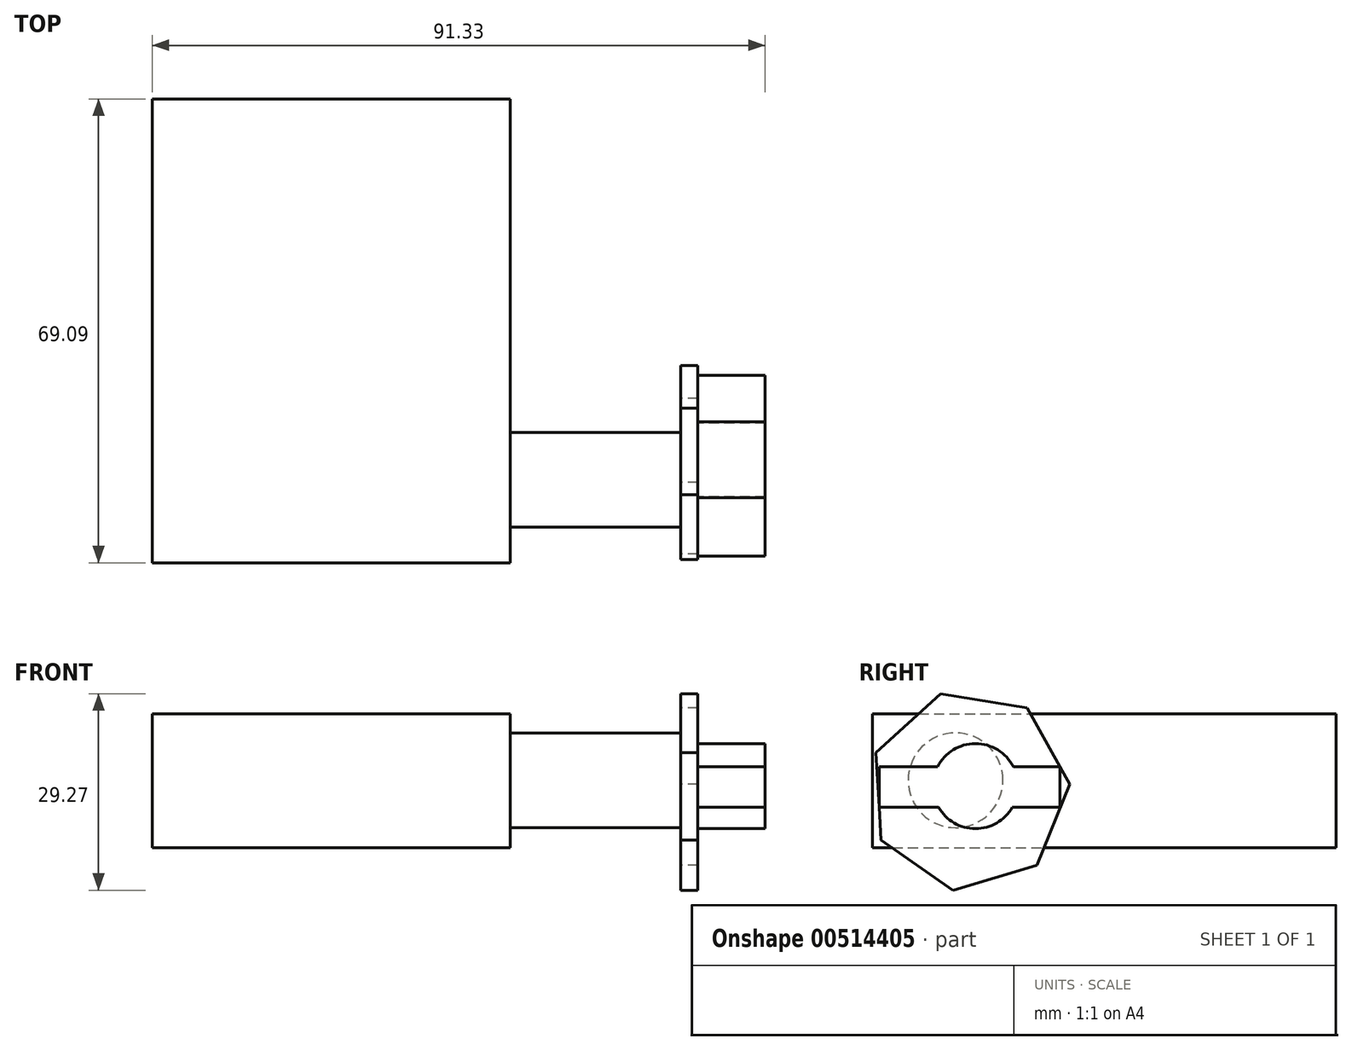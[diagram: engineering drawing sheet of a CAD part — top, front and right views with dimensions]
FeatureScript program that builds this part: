
annotation { "Feature Type Name" : "Feature", "Feature Type Description" : "" }
export const myFeature = defineFeature(function(context is Context, id is Id, definition is map)
    precondition{}
    {
        {
            var Q0;
            Q0=qCreatedBy(makeId("Front.planeOp"),FACE);
            var sketch = newSketch(context, id + "F0", { "sketchPlane" : qUnion([Q0])});
            skLineSegment(sketch, "E0.bottom", {"start": v(-40.49, 8.66) * mm, "end": v(12.87, 8.66) * mm});
            skLineSegment(sketch, "E0.top", {"start": v(-40.49, 28.64) * mm, "end": v(12.87, 28.64) * mm});
            skLineSegment(sketch, "E0.left", {"start": v(-40.49, 8.66) * mm, "end": v(-40.49, 28.64) * mm});
            skLineSegment(sketch, "E0.right", {"start": v(12.87, 8.66) * mm, "end": v(12.87, 28.64) * mm});
            skSolve(sketch);
        }
        {
            var Q0;
            Q0 = qSketchRegion(id + "F0", true);
            extrude(context, id + "F1", {"entities" : qUnion([Q0]), "depth" : 69.1 * mm});
        }
        {
            var Q0;
            Q0=makeQuery(id+"F1.opExtrude","SWEPT_FACE",FACE,{"disambiguationData":[OSD([sQuery(id+"F0.wireOp",EDGE,"E0.right")])]});
            var sketch = newSketch(context, id + "F2", { "sketchPlane" : qUnion([Q0])});
            skCircle(sketch, "E1", {"center": v(-56.73, 18.72) * mm, "radius": 7.06 * mm});
            skSolve(sketch);
        }
        {
            var Q0;
            Q0 = qSketchRegion(id + "F2", true);
            extrude(context, id + "F3", {"entities" : qUnion([Q0]), "operationType" : NewBodyOperationType.ADD, "depth" : 25.4 * mm});
        }
        {
            var Q0;
            Q0=makeQuery(id+"F3.opExtrude","CAP_FACE",FACE,{"disambiguationData":[OSD([sQuery(id+"F2.wireOp",EDGE,"E1")])],"isStart":false});
            var sketch = newSketch(context, id + "F4", { "sketchPlane" : qUnion([Q0])});
            skCircle(sketch, "E2.cCircle", {"center": v(-54.7, 17.2) * mm, "radius": 13.55 * mm, "construction": true});
            skLineSegment(sketch, "E2.0", {"start": v(-58.95, 31.62) * mm, "end": v(-46.07, 29.51) * mm});
            skLineSegment(sketch, "E2.1", {"start": v(-46.07, 29.51) * mm, "end": v(-39.69, 18.13) * mm});
            skLineSegment(sketch, "E2.2", {"start": v(-39.69, 18.13) * mm, "end": v(-44.6, 6.04) * mm});
            skLineSegment(sketch, "E2.3", {"start": v(-44.6, 6.04) * mm, "end": v(-57.12, 2.35) * mm});
            skLineSegment(sketch, "E2.4", {"start": v(-57.12, 2.35) * mm, "end": v(-67.81, 9.84) * mm});
            skLineSegment(sketch, "E2.5", {"start": v(-67.81, 9.84) * mm, "end": v(-68.62, 22.86) * mm});
            skLineSegment(sketch, "E2.6", {"start": v(-68.62, 22.86) * mm, "end": v(-58.95, 31.62) * mm});
            skPoint(sketch, "E2.0.midPoint", {"position": v(-52.5, 30.56) * mm});
            skSolve(sketch);
        }
        {
            var Q0;
            Q0 = qSketchRegion(id + "F4", true);
            extrude(context, id + "F5", {"entities" : qUnion([Q0]), "operationType" : NewBodyOperationType.ADD, "depth" : 2.54 * mm});
        }
        {
            var Q0;
            Q0=makeQuery(id+"F5.opExtrude","CAP_FACE",FACE,{"disambiguationData":[OSD([sQuery(id+"F4.wireOp",EDGE,"E2.0"),sQuery(id+"F4.wireOp",EDGE,"E2.1"),sQuery(id+"F4.wireOp",EDGE,"E2.2"),sQuery(id+"F4.wireOp",EDGE,"E2.3"),sQuery(id+"F4.wireOp",EDGE,"E2.4"),sQuery(id+"F4.wireOp",EDGE,"E2.5"),sQuery(id+"F4.wireOp",EDGE,"E2.6")])],"isStart":false});
            var sketch = newSketch(context, id + "F6", { "sketchPlane" : qUnion([Q0])});
            skCircle(sketch, "E3", {"center": v(-53.77, 17.85) * mm, "radius": 6.34 * mm});
            skLineSegment(sketch, "E4.bottom", {"start": v(-68.11, 14.68) * mm, "end": v(-41.15, 14.68) * mm});
            skLineSegment(sketch, "E4.top", {"start": v(-68.11, 20.74) * mm, "end": v(-41.15, 20.74) * mm});
            skLineSegment(sketch, "E4.left", {"start": v(-68.11, 14.68) * mm, "end": v(-68.11, 20.74) * mm});
            skLineSegment(sketch, "E4.right", {"start": v(-41.15, 14.68) * mm, "end": v(-41.15, 20.74) * mm});
            skSolve(sketch);
        }
        {
            var Q0;
            {var subQ0=sQuery(id+"F6.wireOp",EDGE,"E4.bottom");var subQ1=sQuery(id+"F6.wireOp",EDGE,"E3");var subQ2=makeQuery(id+"F6.imprint","INTERSECT",VERTEX,{"disambiguationData":[OD(0.0)],"derivedFrom":[subQ1,subQ0]});Q0=makeQuery(id+"F6.imprint","IMPRINT",FACE,{"disambiguationData":[TD([[makeQuery(id+"F6.imprint","IMPRINT",EDGE,{"disambiguationData":[TD([[subQ2,-1.0]])],"derivedFrom":subQ1}),1.0]])]});}
            var Q1;
            {var subQ5=sQuery(id+"F6.wireOp",EDGE,"E4.right");Q1=makeQuery(id+"F6.imprint","IMPRINT",FACE,{"disambiguationData":[TD([[makeQuery(id+"F6.imprint","IMPRINT",EDGE,{"derivedFrom":subQ5}),1.0]])]});}
            var Q2;
            {var subQ5=sQuery(id+"F6.wireOp",EDGE,"E4.left");Q2=makeQuery(id+"F6.imprint","IMPRINT",FACE,{"disambiguationData":[TD([[makeQuery(id+"F6.imprint","IMPRINT",EDGE,{"derivedFrom":subQ5}),-1.0]])]});}
            var Q3;
            {var subQ0=sQuery(id+"F6.wireOp",EDGE,"E4.top");var subQ1=sQuery(id+"F6.wireOp",EDGE,"E3");var subQ2=makeQuery(id+"F6.imprint","INTERSECT",VERTEX,{"disambiguationData":[OD(0.0)],"derivedFrom":[subQ1,subQ0]});Q3=makeQuery(id+"F6.imprint","IMPRINT",FACE,{"disambiguationData":[TD([[makeQuery(id+"F6.imprint","IMPRINT",EDGE,{"disambiguationData":[TD([[subQ2,-1.0]])],"derivedFrom":subQ1}),1.0]])]});}
            var Q4;
            {var subQ0=sQuery(id+"F6.wireOp",EDGE,"E4.top");var subQ1=sQuery(id+"F6.wireOp",EDGE,"E3");var subQ2=makeQuery(id+"F6.imprint","INTERSECT",VERTEX,{"disambiguationData":[OD(0.0)],"derivedFrom":[subQ1,subQ0]});Q4=makeQuery(id+"F6.imprint","IMPRINT",FACE,{"disambiguationData":[TD([[makeQuery(id+"F6.imprint","IMPRINT",EDGE,{"disambiguationData":[TD([[subQ2,1.0]])],"derivedFrom":subQ1}),1.0]])]});}
            extrude(context, id + "F7", {"entities" : qUnion([Q0, Q1, Q2, Q3, Q4]), "operationType" : NewBodyOperationType.ADD, "depth" : 10.03 * mm});
        }
    });
